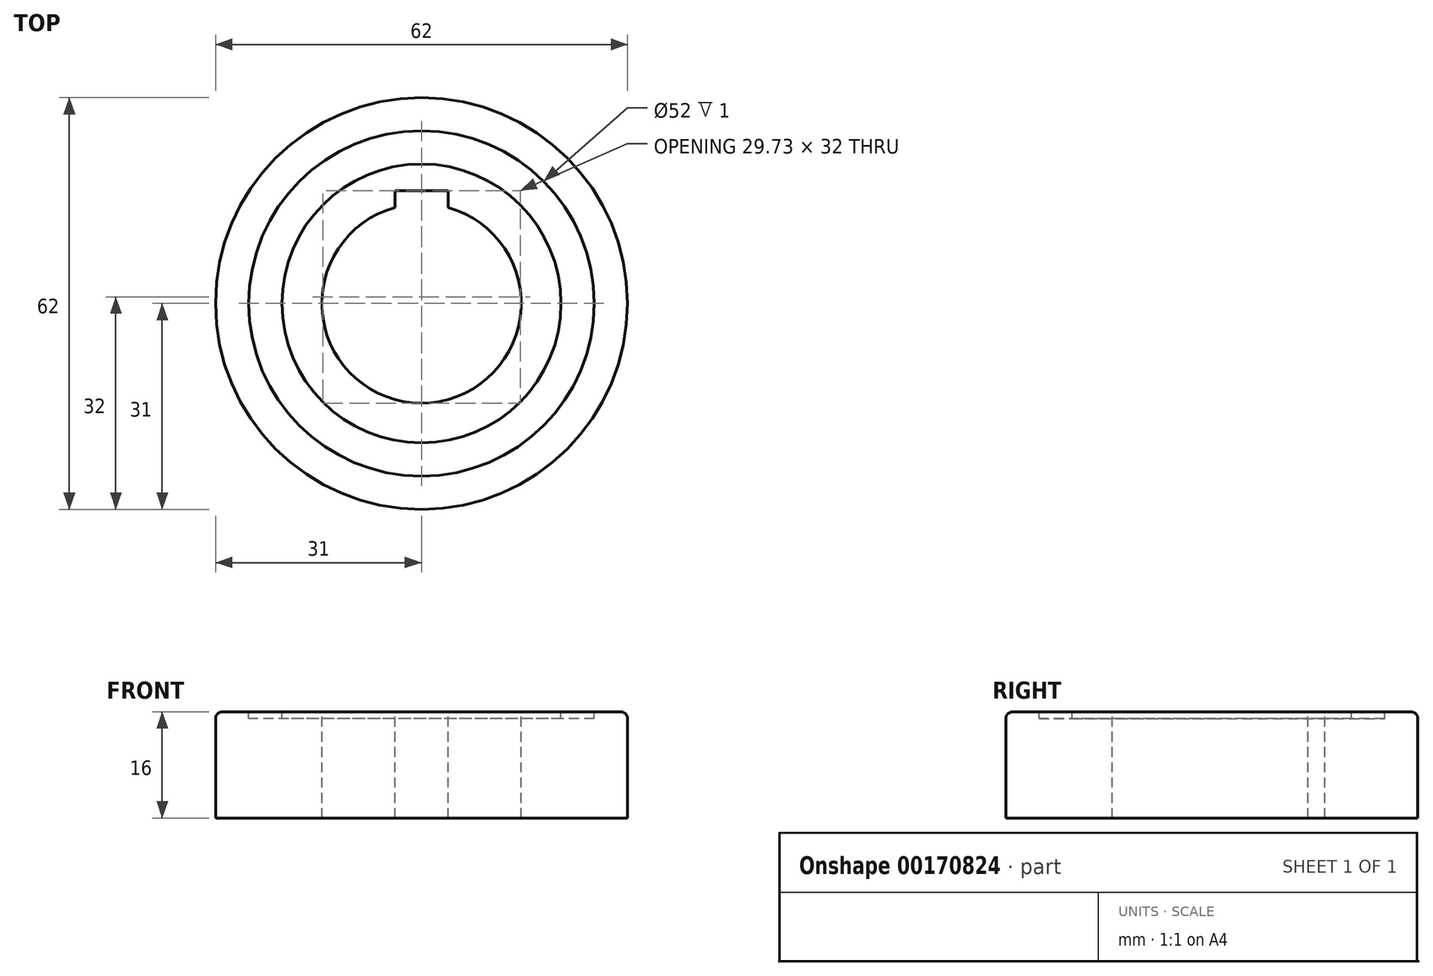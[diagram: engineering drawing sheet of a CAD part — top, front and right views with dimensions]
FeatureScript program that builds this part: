
annotation { "Feature Type Name" : "Feature", "Feature Type Description" : "" }
export const myFeature = defineFeature(function(context is Context, id is Id, definition is map)
    precondition{}
    {
        {
            var Q0;
            Q0=qCreatedBy(makeId("Top.planeOp"),FACE);
            var sketch = newSketch(context, id + "F0", { "sketchPlane" : qUnion([Q0])});
            skCircle(sketch, "E0", {"center": v(0, 0) * mm, "radius": 31 * mm});
            skSolve(sketch);
        }
        {
            var Q0;
            Q0 = qSketchRegion(id + "F0", true);
            extrude(context, id + "F1", {"entities" : qUnion([Q0]), "depth" : 16 * mm});
        }
        {
            var Q0;
            Q0=makeQuery(id+"F1.opExtrude","CAP_FACE",FACE,{"disambiguationData":[OSD([sQuery(id+"F0.wireOp",EDGE,"E0")])],"isStart":false});
            var sketch = newSketch(context, id + "F2", { "sketchPlane" : qUnion([Q0])});
            skCircle(sketch, "E1", {"center": v(0, 0) * mm, "radius": 26 * mm});
            skCircle(sketch, "E2", {"center": v(0, 0) * mm, "radius": 21 * mm});
            skSolve(sketch);
        }
        {
            var Q0;
            Q0 = qSketchRegion(id + "F2", true);
            extrude(context, id + "F3", {"entities" : qUnion([Q0]), "operationType" : NewBodyOperationType.REMOVE, "oppositeDirection" : true, "depth" : 1 * mm});
        }
        {
            var Q0;
            Q0=makeQuery(id+"F3.boolean.opBoolean","SPLIT",FACE,{"disambiguationData":[TD([makeQuery(id+"F3.opExtrude","SWEPT_FACE",FACE,{"disambiguationData":[OSD([sQuery(id+"F2.wireOp",EDGE,"E2")])]})])],"derivedFrom":makeQuery(id+"F1.opExtrude","CAP_FACE",FACE,{"disambiguationData":[OSD([sQuery(id+"F0.wireOp",EDGE,"E0")])],"isStart":false})});
            var sketch = newSketch(context, id + "F4", { "sketchPlane" : qUnion([Q0])});
            skCircle(sketch, "E3", {"center": v(0, 0) * mm, "radius": 15 * mm});
            skSolve(sketch);
        }
        {
            var Q0;
            Q0 = qSketchRegion(id + "F4", true);
            extrude(context, id + "F5", {"entities" : qUnion([Q0]), "operationType" : NewBodyOperationType.REMOVE, "oppositeDirection" : true, "depth" : 25 * mm});
        }
        {
            var Q0;
            Q0=makeQuery(id+"F3.boolean.opBoolean","SPLIT",FACE,{"disambiguationData":[TD([makeQuery(id+"F3.opExtrude","SWEPT_FACE",FACE,{"disambiguationData":[OSD([sQuery(id+"F2.wireOp",EDGE,"E2")])]})])],"derivedFrom":makeQuery(id+"F1.opExtrude","CAP_FACE",FACE,{"disambiguationData":[OSD([sQuery(id+"F0.wireOp",EDGE,"E0")])],"isStart":false})});
            var sketch = newSketch(context, id + "F6", { "sketchPlane" : qUnion([Q0])});
            skLineSegment(sketch, "E4.bottom", {"start": v(-4, 17) * mm, "end": v(4, 17) * mm});
            skLineSegment(sketch, "E4.top", {"start": v(-4, 14) * mm, "end": v(4, 14) * mm});
            skLineSegment(sketch, "E4.left", {"start": v(-4, 17) * mm, "end": v(-4, 14) * mm});
            skLineSegment(sketch, "E4.right", {"start": v(4, 17) * mm, "end": v(4, 14) * mm});
            skSolve(sketch);
        }
        {
            var Q0;
            Q0 = qSketchRegion(id + "F6", true);
            extrude(context, id + "F7", {"entities" : qUnion([Q0]), "operationType" : NewBodyOperationType.REMOVE, "oppositeDirection" : true, "depth" : 25 * mm});
        }
        {
            var Q0;
            Q0=makeQuery(id+"F5.boolean.opBoolean","COPY",EDGE,{"derivedFrom":makeQuery(id+"F5.opExtrude","CAP_EDGE",EDGE,{"disambiguationData":[OSD([sQuery(id+"F4.wireOp",EDGE,"E3")])],"isStart":true})});
            var Q1;
            Q1=makeQuery(id+"F1.opExtrude","CAP_EDGE",EDGE,{"disambiguationData":[OSD([sQuery(id+"F0.wireOp",EDGE,"E0")])],"isStart":false});
            fillet(context, id + "F8", {"entities" : qUnion([Q0, Q1]), "radius" : 1 * mm, "tangentPropagation" : true, "allowEdgeOverflow" : false});
        }
    });
